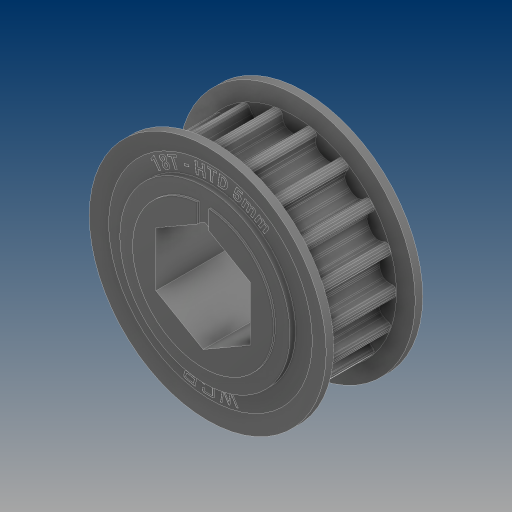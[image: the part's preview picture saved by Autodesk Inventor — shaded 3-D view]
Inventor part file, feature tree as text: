
AUTODESK INVENTOR PART (.ipt)
format: ipt  version: 2024.3 (Build 283343000, 343)  size: 839,168 bytes
history: native  units: in
note: dims shown in document units (in); Inventor stores cm internally (conversion verified against a paired STEP export)
features: mirror x2, other x1
ambient origin geometry x8: Origin, YZ Plane, XZ Plane, XY Plane, X Axis, Y Axis, Z Axis, Center Point
bodies: Solid1 (feature_tree), Solid2 (feature_tree), Solid3 (feature_tree)
feature tree (3):
  mirror  "Mirror2"
  mirror  "Mirror1"
  other  "Cut-Extrude5"
